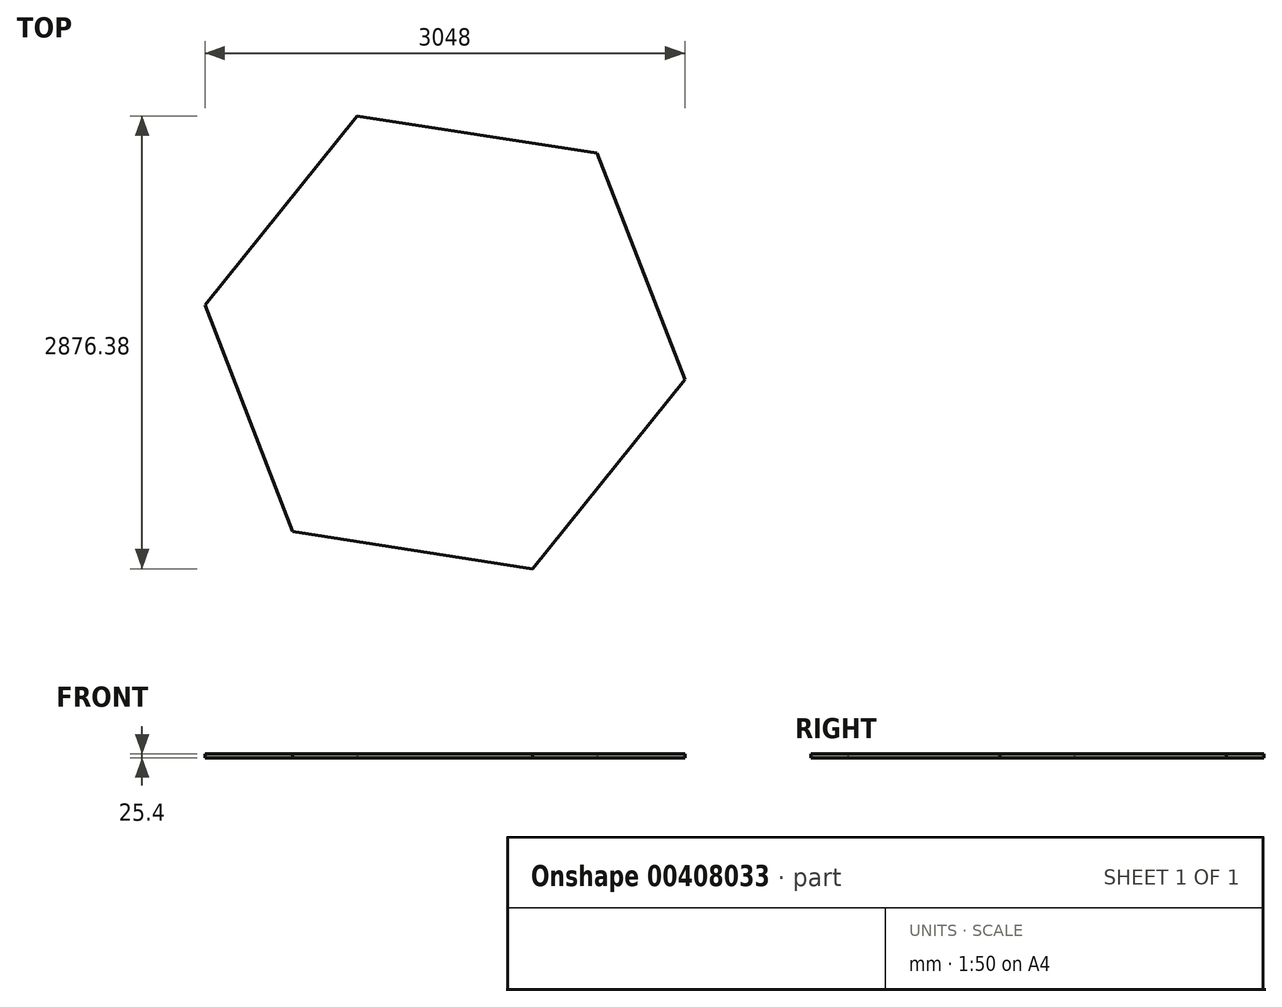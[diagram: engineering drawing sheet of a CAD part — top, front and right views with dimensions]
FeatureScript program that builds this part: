
annotation { "Feature Type Name" : "Feature", "Feature Type Description" : "" }
export const myFeature = defineFeature(function(context is Context, id is Id, definition is map)
    precondition{}
    {
        {
            var Q0;
            Q0=qCreatedBy(makeId("Top.planeOp"),FACE);
            var sketch = newSketch(context, id + "F0", { "sketchPlane" : qUnion([Q0])});
            skCircle(sketch, "E0.cCircle", {"center": v(0, 0) * mm, "radius": 1542.28 * mm, "construction": true});
            skLineSegment(sketch, "E0.0", {"start": v(967.02, 1201.45) * mm, "end": v(1524, -236.74) * mm});
            skLineSegment(sketch, "E0.1", {"start": v(1524, -236.74) * mm, "end": v(556.98, -1438.2) * mm});
            skLineSegment(sketch, "E0.2", {"start": v(556.98, -1438.2) * mm, "end": v(-967.02, -1201.45) * mm});
            skLineSegment(sketch, "E0.3", {"start": v(-967.02, -1201.45) * mm, "end": v(-1524, 236.74) * mm});
            skLineSegment(sketch, "E0.4", {"start": v(-1524, 236.74) * mm, "end": v(-556.98, 1438.2) * mm});
            skLineSegment(sketch, "E0.5", {"start": v(-556.98, 1438.2) * mm, "end": v(967.02, 1201.45) * mm});
            skLineSegment(sketch, "E1", {"start": v(-556.98, 1438.2) * mm, "end": v(1524, -236.74) * mm});
            skSolve(sketch);
        }
        {
            var Q0;
            Q0=makeQuery(id+"F0.imprint","IMPRINT",FACE,{"disambiguationData":[TD([[makeQuery(id+"F0.imprint","IMPRINT",EDGE,{"derivedFrom":sQuery(id+"F0.wireOp",EDGE,"E0.0")}),-1.0]])]});
            var Q1;
            Q1 = qSketchRegion(id + "F0", true);
            var Q2;
            Q2=makeQuery(id+"F0.imprint","IMPRINT",FACE,{"disambiguationData":[TD([[makeQuery(id+"F0.imprint","IMPRINT",EDGE,{"derivedFrom":sQuery(id+"F0.wireOp",EDGE,"E0.1")}),-1.0]])]});
            extrude(context, id + "F1", {"entities" : qUnion([Q0, Q1, Q2]), "depth" : 25.4 * mm});
        }
    });
